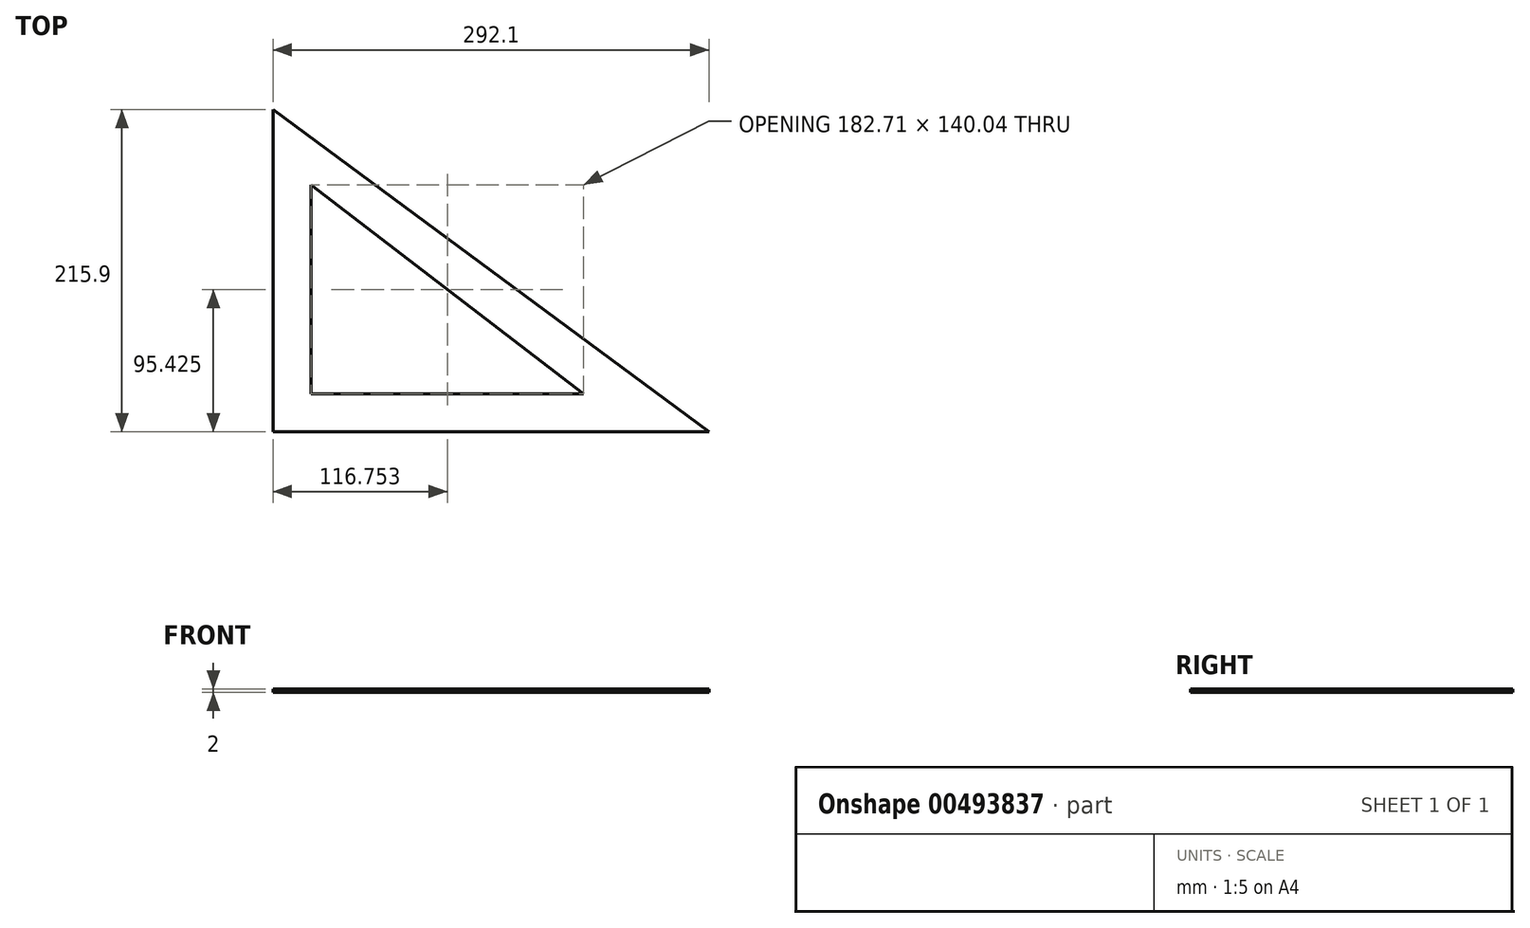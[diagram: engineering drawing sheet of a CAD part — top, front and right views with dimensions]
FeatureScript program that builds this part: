
annotation { "Feature Type Name" : "Feature", "Feature Type Description" : "" }
export const myFeature = defineFeature(function(context is Context, id is Id, definition is map)
    precondition{}
    {
        {
            var Q0;
            Q0=qCreatedBy(makeId("Top.planeOp"),FACE);
            var sketch = newSketch(context, id + "F0", { "sketchPlane" : qUnion([Q0])});
            skLineSegment(sketch, "E0", {"start": v(-110.4, -106.4) * mm, "end": v(-110.4, 109.5) * mm});
            skLineSegment(sketch, "E1", {"start": v(-110.4, 109.5) * mm, "end": v(181.7, -106.4) * mm});
            skLineSegment(sketch, "E2", {"start": v(181.7, -106.4) * mm, "end": v(-110.4, -106.4) * mm});
            skLineSegment(sketch, "E3", {"start": v(-85, 59.05) * mm, "end": v(-85, -81) * mm});
            skLineSegment(sketch, "E4", {"start": v(-85, -81) * mm, "end": v(97.72, -81) * mm});
            skLineSegment(sketch, "E5", {"start": v(97.72, -81) * mm, "end": v(-85, 59.05) * mm});
            skSolve(sketch);
        }
        {
            var Q0;
            Q0=makeQuery(id+"F0.imprint","IMPRINT",FACE,{"disambiguationData":[TD([[makeQuery(id+"F0.imprint","IMPRINT",EDGE,{"derivedFrom":sQuery(id+"F0.wireOp",EDGE,"E0")}),-1.0]])]});
            extrude(context, id + "F1", {"entities" : qUnion([Q0]), "depth" : 2 * mm, "offsetDistance" : 25.4 * mm});
        }
    });
